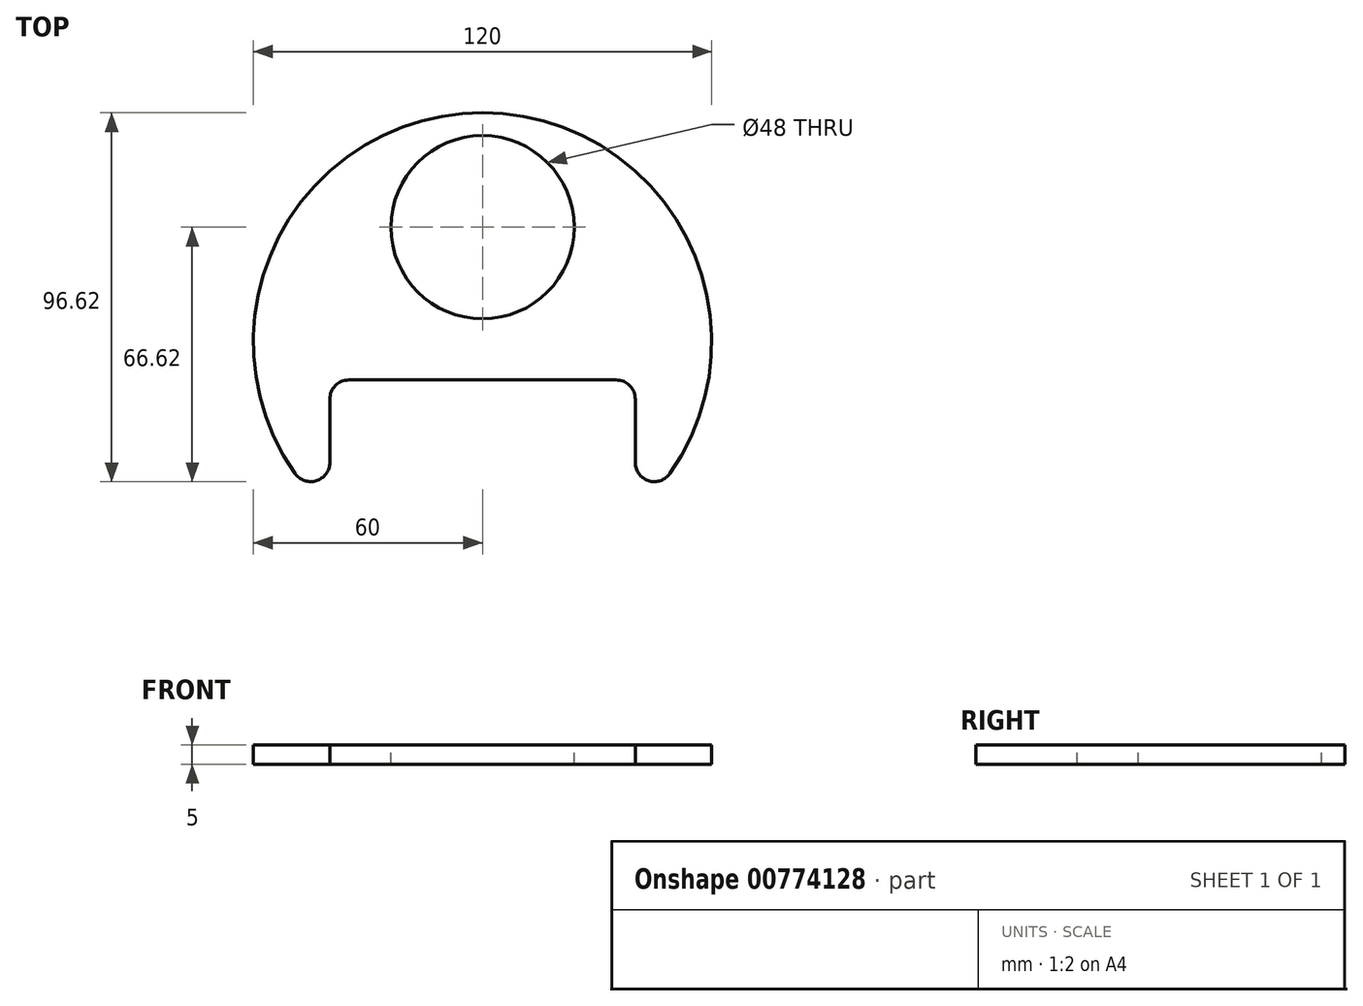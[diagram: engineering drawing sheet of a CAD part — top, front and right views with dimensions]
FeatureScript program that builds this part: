
annotation { "Feature Type Name" : "Feature", "Feature Type Description" : "" }
export const myFeature = defineFeature(function(context is Context, id is Id, definition is map)
    precondition{}
    {
        {
            var Q0;
            Q0=qCreatedBy(makeId("Top.planeOp"),FACE);
            var sketch = newSketch(context, id + "F0", { "sketchPlane" : qUnion([Q0])});
            skCircle(sketch, "E0", {"center": v(0, 0) * mm, "radius": 60 * mm});
            skSolve(sketch);
        }
        {
            var Q0;
            Q0=qCreatedBy(makeId("Top.planeOp"),FACE);
            var sketch = newSketch(context, id + "F1", { "sketchPlane" : qUnion([Q0])});
            skCircle(sketch, "E1", {"center": v(0, 30) * mm, "radius": 24 * mm});
            skSolve(sketch);
        }
        {
            var Q0;
            Q0=qCreatedBy(makeId("Top.planeOp"),FACE);
            var sketch = newSketch(context, id + "F2", { "sketchPlane" : qUnion([Q0])});
            skLineSegment(sketch, "E2.bottom", {"start": v(40, -10) * mm, "end": v(-40, -10) * mm});
            skLineSegment(sketch, "E2.top", {"start": v(40, -90) * mm, "end": v(-40, -90) * mm});
            skLineSegment(sketch, "E2.left", {"start": v(40, -10) * mm, "end": v(40, -90) * mm});
            skLineSegment(sketch, "E2.right", {"start": v(-40, -10) * mm, "end": v(-40, -90) * mm});
            skPoint(sketch, "E2.middle", {"position": v(0, -50) * mm});
            skSolve(sketch);
        }
        {
            var Q0;
            Q0 = qSketchRegion(id + "F0", true);
            extrude(context, id + "F3", {"entities" : qUnion([Q0]), "oppositeDirection" : true, "depth" : 5 * mm, "offsetDistance" : 25 * mm});
        }
        {
            var Q0;
            Q0 = qSketchRegion(id + "F1", true);
            var Q1;
            Q1 = qSketchRegion(id + "F2", true);
            extrude(context, id + "F4", {"entities" : qUnion([Q0, Q1]), "operationType" : NewBodyOperationType.REMOVE, "endBound" : BoundingType.THROUGH_ALL, "oppositeDirection" : true, "depth" : 25 * mm, "offsetDistance" : 25 * mm});
        }
        {
            var Q0;
            Q0=makeQuery(id+"F4.boolean.opBoolean","COPY",EDGE,{"derivedFrom":makeQuery(id+"F4.opExtrude","SWEPT_EDGE",EDGE,{"disambiguationData":[OSD([sQuery(id+"F2.wireOp",EDGE,"E2.bottom"),sQuery(id+"F2.wireOp",EDGE,"E2.right")])]})});
            var Q1;
            Q1=makeQuery(id+"F4.boolean.opBoolean","COPY",EDGE,{"derivedFrom":makeQuery(id+"F4.opExtrude","SWEPT_EDGE",EDGE,{"disambiguationData":[OSD([sQuery(id+"F2.wireOp",EDGE,"E2.bottom"),sQuery(id+"F2.wireOp",EDGE,"E2.left")])]})});
            fillet(context, id + "F5", {"entities" : qUnion([Q0, Q1]), "radius" : 5 * mm, "tangentPropagation" : true, "allowEdgeOverflow" : false});
        }
        {
            var Q0;
            Q0=makeQuery(id+"F4.boolean.opBoolean","INTERSECT",EDGE,{"derivedFrom":[makeQuery(id+"F3.opExtrude","SWEPT_FACE",FACE,{"disambiguationData":[OSD([sQuery(id+"F0.wireOp",EDGE,"E0")])]}),makeQuery(id+"F4.opExtrude","SWEPT_FACE",FACE,{"disambiguationData":[OSD([sQuery(id+"F2.wireOp",EDGE,"E2.right")])]})]});
            var Q1;
            Q1=makeQuery(id+"F4.boolean.opBoolean","INTERSECT",EDGE,{"derivedFrom":[makeQuery(id+"F3.opExtrude","SWEPT_FACE",FACE,{"disambiguationData":[OSD([sQuery(id+"F0.wireOp",EDGE,"E0")])]}),makeQuery(id+"F4.opExtrude","SWEPT_FACE",FACE,{"disambiguationData":[OSD([sQuery(id+"F2.wireOp",EDGE,"E2.left")])]})]});
            fillet(context, id + "F6", {"entities" : qUnion([Q0, Q1]), "radius" : 5 * mm, "tangentPropagation" : true, "allowEdgeOverflow" : false});
        }
    });
